FCSTD DOCUMENT  (FreeCAD 1.0R39319 (Git))
Label: demo1
License: All rights reserved
LicenseURL: https://en.wikipedia.org/wiki/All_rights_reserved
objects: Sketcher::SketchObject×2, PartDesign::Body×1
note: 5 computed .brp shape members not serialized (recipe doc carries the construction recipe); baked Part::Feature solids carry a one-line shape summary decoded from their .brp

FEATURE [Sketcher::SketchObject] Sketch
  ArcFitTolerance = 1e-06
  AttachmentSupport = -> [XY_Plane]
  FullyConstrained = false
  MakeInternals = false
  MapMode = 5
  sketch-geometry (4):
    g0: LineSegment StartX=-58.0347 StartY=48.1698 StartZ=0 EndX=-58.0347 EndY=0 EndZ=0
    g1: LineSegment StartX=-58.0347 StartY=0 StartZ=0 EndX=53.7517 EndY=0 EndZ=0
    g2: LineSegment StartX=53.7517 StartY=0 StartZ=0 EndX=53.7517 EndY=48.1698 EndZ=0
    g3: LineSegment StartX=53.7517 StartY=48.1698 StartZ=0 EndX=-58.0347 EndY=48.1698 EndZ=0
  constraints (9):
    c: Coincident(g0,g1)
    c: Coincident(g1,g2)
    c: Coincident(g2,g3)
    c: Coincident(g3,g0)
    c: Vertical(g0)
    c: Vertical(g2)
    c: Horizontal(g1)
    c: Horizontal(g3)
    c: PointOnObject(g1,g-1)
FEATURE [Sketcher::SketchObject] Sketch001
  ArcFitTolerance = 1e-06
  AttachmentSupport = -> [XY_Plane]
  FullyConstrained = false
  MakeInternals = false
  MapMode = 5
  sketch-geometry (7):
    g0: LineSegment StartX=-33.9549 StartY=-2.6372 StartZ=0 EndX=-33.9549 EndY=-52.6372 EndZ=0
    g1: LineSegment StartX=-33.9549 StartY=-52.6372 StartZ=0 EndX=-17.2097 EndY=-52.6372 EndZ=0
    g2: LineSegment StartX=33.9549 StartY=-47.3628 StartZ=0 EndX=33.9549 EndY=2.6372 EndZ=0
    g3: Circle [constr] CenterX=2.6e-15 CenterY=-50 CenterZ=0 NormalX=0 NormalY=0 NormalZ=1 AngleXU=0 Radius=8.76403
    g4: ArcOfCircle CenterX=2.6e-15 CenterY=-50 CenterZ=0 NormalX=0 NormalY=0 NormalZ=1 AngleXU=0 Radius=17.4106 StartAngle=3.29365 EndAngle=6.43524
    g5: LineSegment StartX=17.2097 StartY=-47.3628 StartZ=0 EndX=33.9549 EndY=-47.3628 EndZ=0
    g6: LineSegment StartX=-7.67057e-06 StartY=-41.236 StartZ=0 EndX=3.7e-15 EndY=-41.236 EndZ=0
  constraints (17):
    c: Coincident(g0,g1)
    c: Coincident(g5,g2)
    c: Vertical(g0)
    c: Vertical(g2)
    c: Horizontal(g1)
    c: Symmetric(g0,g2,g-1)
    c: Symmetric(g1,g5,g3)
    c: Coincident(g4,g3)
    c: PointOnObject(g4,g5)
    c: PointOnObject(g5,g4)
    c: Coincident(g1,g4)
    c: PointOnObject(g6,g3)
    c: DistanceY(g0,g0) = 50
    c: DistanceY(g2,g2) = 50
    c: Horizontal(g6)
    c: Tangent(g6,g3) = 1.5708
    c: Equal(g5,g1)
FEATURE [PartDesign::Body] Body
  AllowCompound = false
  Group = -> [Sketch,Sketch001]
  Origin = -> Origin
